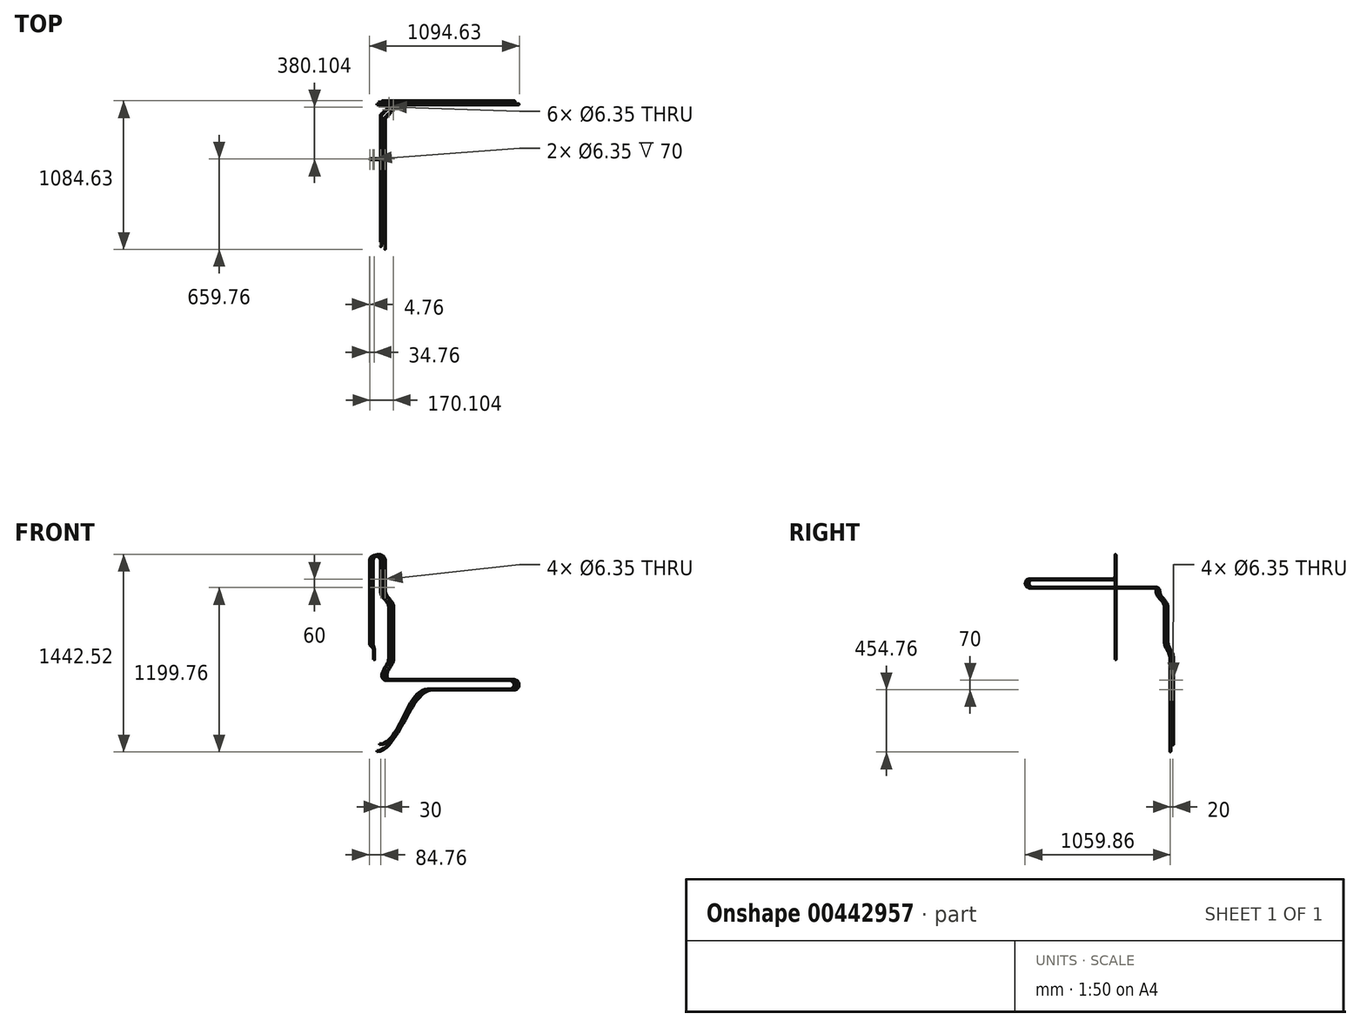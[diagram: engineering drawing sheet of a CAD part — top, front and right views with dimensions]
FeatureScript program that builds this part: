
annotation { "Feature Type Name" : "Feature", "Feature Type Description" : "" }
export const myFeature = defineFeature(function(context is Context, id is Id, definition is map)
    precondition{}
    {
        {
            var Q0;
            Q0=qCreatedBy(makeId("Top.planeOp"),FACE);
            var sketch = newSketch(context, id + "F0", { "sketchPlane" : qUnion([Q0])});
            skCircle(sketch, "E0", {"center": v(0, 0) * mm, "radius": 4.76 * mm});
            skCircle(sketch, "E1", {"center": v(0, 0) * mm, "radius": 3.17 * mm});
            skSolve(sketch);
        }
        {
            var Q0;
            Q0=qCreatedBy(makeId("Front.planeOp"),FACE);
            var sketch = newSketch(context, id + "F1", { "sketchPlane" : qUnion([Q0])});
            skLineSegment(sketch, "E2", {"start": v(80, 612) * mm, "end": v(80, 720) * mm});
            skArc(sketch, "E3", {"start": v(80, 720) * mm, "mid": v(35, 765) * mm, "end": v(-10, 720) * mm});
            skLineSegment(sketch, "E4", {"start": v(0, 70) * mm, "end": v(0, 0) * mm});
            skFitSpline(sketch, "E5", {"points": [v(0, 70) * mm, v(-5, 95) * mm, v(-10, 120) * mm], "startDerivative": vector(0, 60) * mm, "endDerivative": vector(0, 60) * mm});
            skLineSegment(sketch, "E6", {"start": v(-10, 110) * mm, "end": v(-10, 120) * mm, "construction": true});
            skLineSegment(sketch, "E7", {"start": v(0, 80) * mm, "end": v(0, 70) * mm, "construction": true});
            skLineSegment(sketch, "E8", {"start": v(0, 70) * mm, "end": v(-10, 120) * mm, "construction": true});
            skLineSegment(sketch, "E9", {"start": v(-10, 120) * mm, "end": v(-10, 720) * mm});
            skSolve(sketch);
        }
        {
            var Q0;
            Q0=qCreatedBy(makeId("Right.planeOp"),FACE);
            var Q1;
            Q1=sQuery(id+"F1.wireOp",VERTEX,"E2.start");
            cPlane(context, id + "F2", {"entities" : qUnion([Q0, Q1]), "cplaneType" : CPlaneType.PLANE_POINT, "offset" : 25 * mm, "width" : 150 * mm, "height" : 150 * mm});
        }
        {
            var Q0;
            Q0=qCreatedBy(id+"F2.planeOp",FACE);
            var sketch = newSketch(context, id + "F3", { "sketchPlane" : qUnion([Q0])});
            skArc(sketch, "E10.MirrorCS", {"start": v(0, 612) * mm, "mid": v(-7.32, 594.32) * mm, "end": v(-25, 587) * mm});
            skArc(sketch, "E11.MirrorCS", {"start": v(275, 527) * mm, "mid": v(292.68, 519.68) * mm, "end": v(300, 502) * mm});
            skLineSegment(sketch, "E12.MirrorCS", {"start": v(300, 502) * mm, "end": v(300, 517.1) * mm, "construction": true});
            skLineSegment(sketch, "E13.MirrorCS", {"start": v(-25, 587) * mm, "end": v(-625, 587) * mm});
            skArc(sketch, "E14.MirrorCS", {"start": v(-625, 527) * mm, "mid": v(-655, 557) * mm, "end": v(-625, 587) * mm});
            skLineSegment(sketch, "E15.MirrorCS", {"start": v(-625, 527) * mm, "end": v(275, 527) * mm});
            skSolve(sketch);
        }
        {
            var Q0;
            Q0=sQuery(id+"F3.wireOp",EDGE,"E12.MirrorCS");
            cPlane(context, id + "F4", {"entities" : qUnion([Q0]), "cplaneType" : CPlaneType.LINE_ANGLE, "offset" : 25 * mm, "angle" : 45 * degree, "oppositeDirection" : true, "width" : 150 * mm, "height" : 150 * mm});
        }
        {
            var Q0;
            Q0=qCreatedBy(id+"F4.planeOp",FACE);
            var sketch = newSketch(context, id + "F5", { "sketchPlane" : qUnion([Q0])});
            skFitSpline(sketch, "E16", {"points": [v(268.7, 502) * mm, v(311.2, 442) * mm, v(353.7, 382) * mm], "startDerivative": vector(0, -150) * mm, "endDerivative": vector(0, -150) * mm});
            skLineSegment(sketch, "E17", {"start": v(268.7, 477) * mm, "end": v(268.7, 502) * mm, "construction": true});
            skLineSegment(sketch, "E18", {"start": v(353.7, 407) * mm, "end": v(353.7, 382) * mm, "construction": true});
            skLineSegment(sketch, "E19", {"start": v(353.7, 382) * mm, "end": v(268.7, 502) * mm, "construction": true});
            skLineSegment(sketch, "E20", {"start": v(353.7, 382) * mm, "end": v(353.7, 132) * mm});
            skSolve(sketch);
        }
        {
            var Q0;
            Q0=qCreatedBy(makeId("Right.planeOp"),FACE);
            var Q1;
            Q1=sQuery(id+"F5.wireOp",VERTEX,"E20.end");
            cPlane(context, id + "F6", {"entities" : qUnion([Q0, Q1]), "cplaneType" : CPlaneType.PLANE_POINT, "offset" : 25 * mm, "width" : 150 * mm, "height" : 150 * mm});
        }
        {
            var Q0;
            Q0=qCreatedBy(id+"F6.planeOp",FACE);
            var sketch = newSketch(context, id + "F7", { "sketchPlane" : qUnion([Q0])});
            skFitSpline(sketch, "E21", {"points": [v(360.1, 132) * mm, v(380.1, 72) * mm, v(400.1, 12) * mm], "startDerivative": vector(0, -150) * mm, "endDerivative": vector(0, -150) * mm});
            skLineSegment(sketch, "E22", {"start": v(360.1, 132) * mm, "end": v(360.1, 107) * mm, "construction": true});
            skLineSegment(sketch, "E23", {"start": v(400.1, 37) * mm, "end": v(400.1, 12) * mm, "construction": true});
            skLineSegment(sketch, "E24", {"start": v(400.1, 12) * mm, "end": v(360.1, 132) * mm, "construction": true});
            skSolve(sketch);
        }
        {
            var Q0;
            Q0=sQuery(id+"F7.wireOp",VERTEX,"E21.end");
            var Q1;
            Q1=qCreatedBy(makeId("Front.planeOp"),FACE);
            cPlane(context, id + "F8", {"entities" : qUnion([Q0, Q1]), "cplaneType" : CPlaneType.PLANE_POINT, "offset" : 25 * mm, "width" : 150 * mm, "height" : 150 * mm});
        }
        {
            var Q0;
            Q0=qCreatedBy(id+"F8.planeOp",FACE);
            var sketch = newSketch(context, id + "F9", { "sketchPlane" : qUnion([Q0])});
            skFitSpline(sketch, "E25", {"points": [v(140.1, 12) * mm, v(115.1, -53) * mm, v(90.1, -118) * mm], "startDerivative": vector(0, -150) * mm, "endDerivative": vector(0, -150) * mm});
            skLineSegment(sketch, "E26", {"start": v(140.1, 12) * mm, "end": v(140.1, -13) * mm, "construction": true});
            skLineSegment(sketch, "E27", {"start": v(90.1, -93) * mm, "end": v(90.1, -118) * mm, "construction": true});
            skLineSegment(sketch, "E28", {"start": v(90.1, -118) * mm, "end": v(140.1, 12) * mm, "construction": true});
            skArc(sketch, "E29", {"start": v(90.1, -118) * mm, "mid": v(98.9, -139.21) * mm, "end": v(120.1, -148) * mm});
            skLineSegment(sketch, "E30", {"start": v(120.1, -148) * mm, "end": v(1020.1, -148) * mm});
            skArc(sketch, "E31", {"start": v(1020.1, -218) * mm, "mid": v(1055.1, -183) * mm, "end": v(1020.1, -148) * mm});
            skLineSegment(sketch, "E32", {"start": v(1020.1, -218) * mm, "end": v(420.1, -218) * mm});
            skFitSpline(sketch, "E33", {"points": [v(420.1, -218) * mm, v(220.1, -443) * mm, v(20.1, -668) * mm], "startDerivative": vector(-450, 0) * mm, "endDerivative": vector(-450, 0) * mm});
            skLineSegment(sketch, "E34", {"start": v(420.1, -218) * mm, "end": v(345.1, -218) * mm, "construction": true});
            skLineSegment(sketch, "E35", {"start": v(95.1, -668) * mm, "end": v(20.1, -668) * mm, "construction": true});
            skLineSegment(sketch, "E36", {"start": v(20.1, -668) * mm, "end": v(420.1, -218) * mm, "construction": true});
            skSolve(sketch);
        }
        {
            var Q0;
            Q0=qSketchRegion(id+"F0",true);
            var Q1;
            Q1=qConstructionFilter(qBodyType(qCreatedBy(id+"F1",EDGE),BodyType.WIRE),ConstructionObject.NO);
            var Q2;
            Q2=qConstructionFilter(qBodyType(qCreatedBy(id+"F3",EDGE),BodyType.WIRE),ConstructionObject.NO);
            var Q3;
            Q3=qConstructionFilter(qBodyType(qCreatedBy(id+"F5",EDGE),BodyType.WIRE),ConstructionObject.NO);
            var Q4;
            Q4=qConstructionFilter(qBodyType(qCreatedBy(id+"F7",EDGE),BodyType.WIRE),ConstructionObject.NO);
            var Q5;
            Q5=qConstructionFilter(qBodyType(qCreatedBy(id+"F9",EDGE),BodyType.WIRE),ConstructionObject.NO);
            sweep(context, id + "F10", {"profiles" : qUnion([Q0]), "path" : qUnion([Q1, Q2, Q3, Q4, Q5])});
        }
        {
            var Q0;
            Q0=qCreatedBy(makeId("Front.planeOp"),FACE);
            var sketch = newSketch(context, id + "F11", { "sketchPlane" : qUnion([Q0])});
            skLineSegment(sketch, "E37", {"start": v(50, 612) * mm, "end": v(50, 720) * mm});
            skArc(sketch, "E38", {"start": v(50, 720) * mm, "mid": v(10, 760) * mm, "end": v(-30, 720) * mm});
            skLineSegment(sketch, "E39", {"start": v(0, 70) * mm, "end": v(0, 0) * mm});
            skFitSpline(sketch, "E40", {"points": [v(0, 70) * mm, v(-15, 95) * mm, v(-30, 120) * mm], "startDerivative": vector(0, 60) * mm, "endDerivative": vector(0, 60) * mm});
            skLineSegment(sketch, "E41", {"start": v(-30, 110) * mm, "end": v(-30, 120) * mm, "construction": true});
            skLineSegment(sketch, "E42", {"start": v(0, 80) * mm, "end": v(0, 70) * mm, "construction": true});
            skLineSegment(sketch, "E43", {"start": v(0, 70) * mm, "end": v(-30, 120) * mm, "construction": true});
            skLineSegment(sketch, "E44", {"start": v(-30, 120) * mm, "end": v(-30, 720) * mm});
            skSolve(sketch);
        }
        {
            var Q0;
            Q0=qCreatedBy(makeId("Right.planeOp"),FACE);
            var Q1;
            Q1=sQuery(id+"F11.wireOp",VERTEX,"E37.start");
            cPlane(context, id + "F12", {"entities" : qUnion([Q0, Q1]), "cplaneType" : CPlaneType.PLANE_POINT, "offset" : 25 * mm, "width" : 150 * mm, "height" : 150 * mm});
        }
        {
            var Q0;
            Q0=qCreatedBy(id+"F12.planeOp",FACE);
            var sketch = newSketch(context, id + "F13", { "sketchPlane" : qUnion([Q0])});
            skArc(sketch, "E45.MirrorCS", {"start": v(0, 612) * mm, "mid": v(-7.32, 594.32) * mm, "end": v(-25, 587) * mm});
            skArc(sketch, "E46.MirrorCS", {"start": v(295, 527) * mm, "mid": v(312.68, 519.68) * mm, "end": v(320, 502) * mm});
            skLineSegment(sketch, "E47.MirrorCS", {"start": v(320, 502) * mm, "end": v(320, 517.1) * mm, "construction": true});
            skLineSegment(sketch, "E48.MirrorCS", {"start": v(-25, 587) * mm, "end": v(-605, 587) * mm});
            skArc(sketch, "E49.MirrorCS", {"start": v(-605, 527) * mm, "mid": v(-635, 557) * mm, "end": v(-605, 587) * mm});
            skLineSegment(sketch, "E50.MirrorCS", {"start": v(-605, 527) * mm, "end": v(295, 527) * mm});
            skSolve(sketch);
        }
        {
            var Q0;
            Q0=sQuery(id+"F13.wireOp",EDGE,"E47.MirrorCS");
            cPlane(context, id + "F14", {"entities" : qUnion([Q0]), "cplaneType" : CPlaneType.LINE_ANGLE, "offset" : 25 * mm, "angle" : 45 * degree, "oppositeDirection" : true, "width" : 150 * mm, "height" : 150 * mm});
        }
        {
            var Q0;
            Q0=qCreatedBy(id+"F14.planeOp",FACE);
            var sketch = newSketch(context, id + "F15", { "sketchPlane" : qUnion([Q0])});
            skFitSpline(sketch, "E51", {"points": [v(261.63, 502) * mm, v(304.13, 442) * mm, v(346.63, 382) * mm], "startDerivative": vector(0, -150) * mm, "endDerivative": vector(0, -150) * mm});
            skLineSegment(sketch, "E52", {"start": v(261.63, 477) * mm, "end": v(261.63, 502) * mm, "construction": true});
            skLineSegment(sketch, "E53", {"start": v(346.63, 407) * mm, "end": v(346.63, 382) * mm, "construction": true});
            skLineSegment(sketch, "E54", {"start": v(346.63, 382) * mm, "end": v(261.63, 502) * mm, "construction": true});
            skLineSegment(sketch, "E55", {"start": v(346.63, 382) * mm, "end": v(346.63, 132) * mm});
            skSolve(sketch);
        }
        {
            var Q0;
            Q0=qCreatedBy(makeId("Right.planeOp"),FACE);
            var Q1;
            Q1=sQuery(id+"F15.wireOp",VERTEX,"E55.end");
            cPlane(context, id + "F16", {"entities" : qUnion([Q0, Q1]), "cplaneType" : CPlaneType.PLANE_POINT, "offset" : 25 * mm, "width" : 150 * mm, "height" : 150 * mm});
        }
        {
            var Q0;
            Q0=qCreatedBy(id+"F16.planeOp",FACE);
            var sketch = newSketch(context, id + "F17", { "sketchPlane" : qUnion([Q0])});
            skFitSpline(sketch, "E56", {"points": [v(380.1, 132) * mm, v(400.1, 72) * mm, v(420.1, 12) * mm], "startDerivative": vector(0, -150) * mm, "endDerivative": vector(0, -150) * mm});
            skLineSegment(sketch, "E57", {"start": v(380.1, 132) * mm, "end": v(380.1, 107) * mm, "construction": true});
            skLineSegment(sketch, "E58", {"start": v(420.1, 37) * mm, "end": v(420.1, 12) * mm, "construction": true});
            skLineSegment(sketch, "E59", {"start": v(420.1, 12) * mm, "end": v(380.1, 132) * mm, "construction": true});
            skSolve(sketch);
        }
        {
            var Q0;
            Q0=qCreatedBy(makeId("Front.planeOp"),FACE);
            var Q1;
            Q1=sQuery(id+"F17.wireOp",VERTEX,"E56.end");
            cPlane(context, id + "F18", {"entities" : qUnion([Q0, Q1]), "cplaneType" : CPlaneType.PLANE_POINT, "offset" : 25 * mm, "width" : 150 * mm, "height" : 150 * mm});
        }
        {
            var Q0;
            Q0=qCreatedBy(id+"F18.planeOp",FACE);
            var sketch = newSketch(context, id + "F19", { "sketchPlane" : qUnion([Q0])});
            skFitSpline(sketch, "E60", {"points": [v(110.1, 12) * mm, v(85.1, -53) * mm, v(60.1, -118) * mm], "startDerivative": vector(0, -150) * mm, "endDerivative": vector(0, -150) * mm});
            skLineSegment(sketch, "E61", {"start": v(110.1, 12) * mm, "end": v(110.1, -13) * mm, "construction": true});
            skLineSegment(sketch, "E62", {"start": v(60.1, -93) * mm, "end": v(60.1, -118) * mm, "construction": true});
            skLineSegment(sketch, "E63", {"start": v(60.1, -118) * mm, "end": v(110.1, 12) * mm, "construction": true});
            skArc(sketch, "E64", {"start": v(60.1, -118) * mm, "mid": v(68.9, -139.21) * mm, "end": v(90.1, -148) * mm});
            skLineSegment(sketch, "E65", {"start": v(90.1, -148) * mm, "end": v(990.1, -148) * mm});
            skArc(sketch, "E66", {"start": v(990.1, -218) * mm, "mid": v(1025.1, -183) * mm, "end": v(990.1, -148) * mm});
            skLineSegment(sketch, "E67", {"start": v(990.1, -218) * mm, "end": v(390.1, -218) * mm});
            skFitSpline(sketch, "E68", {"points": [v(390.1, -218) * mm, v(215.1, -418) * mm, v(40.1, -618) * mm], "startDerivative": vector(-450, 0) * mm, "endDerivative": vector(-450, 0) * mm});
            skLineSegment(sketch, "E69", {"start": v(390.1, -218) * mm, "end": v(315.1, -218) * mm, "construction": true});
            skLineSegment(sketch, "E70", {"start": v(115.1, -618) * mm, "end": v(40.1, -618) * mm, "construction": true});
            skLineSegment(sketch, "E71", {"start": v(40.1, -618) * mm, "end": v(390.1, -218) * mm, "construction": true});
            skSolve(sketch);
        }
        {
            var Q0;
            Q0=qSketchRegion(id+"F0",true);
            var Q1;
            Q1=qConstructionFilter(qBodyType(qCreatedBy(id+"F11",EDGE),BodyType.WIRE),ConstructionObject.NO);
            var Q2;
            Q2=qConstructionFilter(qBodyType(qCreatedBy(id+"F13",EDGE),BodyType.WIRE),ConstructionObject.NO);
            var Q3;
            Q3=qConstructionFilter(qBodyType(qCreatedBy(id+"F15",EDGE),BodyType.WIRE),ConstructionObject.NO);
            var Q4;
            Q4=qConstructionFilter(qBodyType(qCreatedBy(id+"F17",EDGE),BodyType.WIRE),ConstructionObject.NO);
            var Q5;
            Q5=qConstructionFilter(qBodyType(qCreatedBy(id+"F19",EDGE),BodyType.WIRE),ConstructionObject.NO);
            sweep(context, id + "F20", {"profiles" : qUnion([Q0]), "path" : qUnion([Q1, Q2, Q3, Q4, Q5])});
        }
    });
